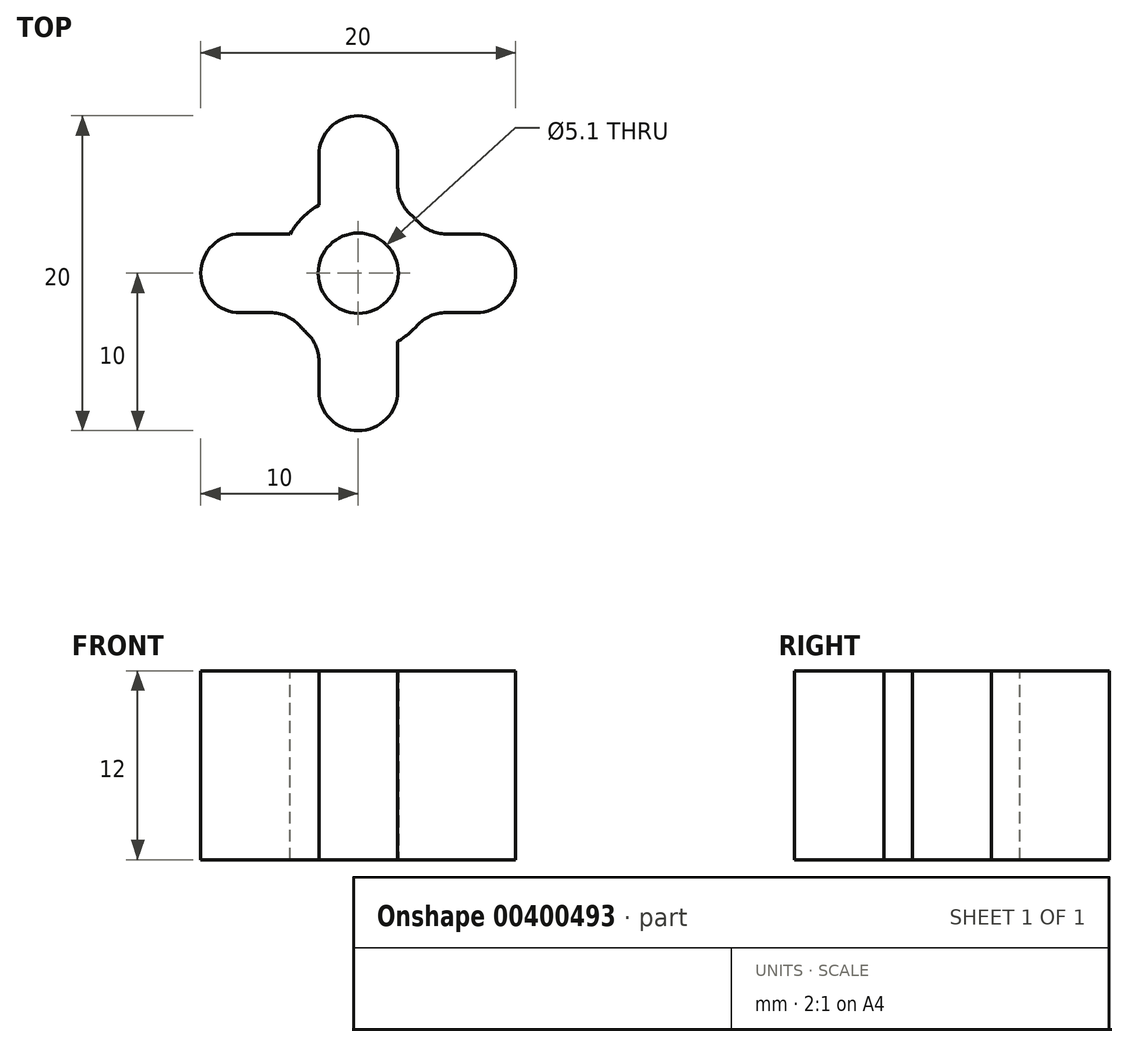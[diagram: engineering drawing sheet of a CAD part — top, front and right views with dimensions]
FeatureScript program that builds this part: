
annotation { "Feature Type Name" : "Feature", "Feature Type Description" : "" }
export const myFeature = defineFeature(function(context is Context, id is Id, definition is map)
    precondition{}
    {
        {
            var Q0;
            Q0=qCreatedBy(makeId("Top.planeOp"),FACE);
            var sketch = newSketch(context, id + "F0", { "sketchPlane" : qUnion([Q0])});
            skCircle(sketch, "E0", {"center": v(0, 0) * mm, "radius": 2.55 * mm});
            skCircle(sketch, "E1", {"center": v(0, 0) * mm, "radius": 5 * mm});
            skSolve(sketch);
        }
        {
            var Q0;
            Q0 = qSketchRegion(id + "F0", true);
            extrude(context, id + "F1", {"entities" : qUnion([Q0]), "depth" : 12 * mm});
        }
        {
            var Q0;
            Q0=makeQuery(id+"F1.opExtrude","CAP_FACE",FACE,{"disambiguationData":[OSD([sQuery(id+"F0.wireOp",EDGE,"E0"),sQuery(id+"F0.wireOp",EDGE,"E1")])],"isStart":false});
            var sketch = newSketch(context, id + "F2", { "sketchPlane" : qUnion([Q0])});
            skLineSegment(sketch, "E2.bottom", {"start": v(-2.5, 4.33) * mm, "end": v(2.5, 4.33) * mm});
            skLineSegment(sketch, "E2.top", {"start": v(-2.5, 10) * mm, "end": v(2.5, 10) * mm});
            skLineSegment(sketch, "E2.left", {"start": v(-2.5, 4.33) * mm, "end": v(-2.5, 10) * mm});
            skLineSegment(sketch, "E2.right", {"start": v(2.5, 4.33) * mm, "end": v(2.5, 10) * mm});
            skLineSegment(sketch, "E3.1.0", {"start": v(-4.33, -2.5) * mm, "end": v(-4.33, 2.5) * mm});
            skLineSegment(sketch, "E3.1.1", {"start": v(-10, -2.5) * mm, "end": v(-10, 2.5) * mm});
            skLineSegment(sketch, "E3.1.2", {"start": v(-4.33, -2.5) * mm, "end": v(-10, -2.5) * mm});
            skLineSegment(sketch, "E3.1.3", {"start": v(-4.33, 2.5) * mm, "end": v(-10, 2.5) * mm});
            skLineSegment(sketch, "E3.2.0", {"start": v(2.5, -4.33) * mm, "end": v(-2.5, -4.33) * mm});
            skLineSegment(sketch, "E3.2.1", {"start": v(2.5, -10) * mm, "end": v(-2.5, -10) * mm});
            skLineSegment(sketch, "E3.2.2", {"start": v(2.5, -4.33) * mm, "end": v(2.5, -10) * mm});
            skLineSegment(sketch, "E3.2.3", {"start": v(-2.5, -4.33) * mm, "end": v(-2.5, -10) * mm});
            skLineSegment(sketch, "E3.3.0", {"start": v(4.33, 2.5) * mm, "end": v(4.33, -2.5) * mm});
            skLineSegment(sketch, "E3.3.1", {"start": v(10, 2.5) * mm, "end": v(10, -2.5) * mm});
            skLineSegment(sketch, "E3.3.2", {"start": v(4.33, 2.5) * mm, "end": v(10, 2.5) * mm});
            skLineSegment(sketch, "E3.3.3", {"start": v(4.33, -2.5) * mm, "end": v(10, -2.5) * mm});
            skPoint(sketch, "E3.center", {"position": v(0, 0) * mm});
            skSolve(sketch);
        }
        {
            var Q0;
            Q0=makeQuery(id+"F2.imprint","IMPRINT",FACE,{"disambiguationData":[TD([[makeQuery(id+"F2.imprint","IMPRINT",EDGE,{"derivedFrom":sQuery(id+"F2.wireOp",EDGE,"E2.top")}),-1.0]])]});
            var Q1;
            Q1=makeQuery(id+"F2.imprint","IMPRINT",FACE,{"disambiguationData":[TD([[makeQuery(id+"F2.imprint","IMPRINT",EDGE,{"derivedFrom":sQuery(id+"F2.wireOp",EDGE,"E3.3.1")}),-1.0]])]});
            var Q2;
            Q2=makeQuery(id+"F2.imprint","IMPRINT",FACE,{"disambiguationData":[TD([[makeQuery(id+"F2.imprint","IMPRINT",EDGE,{"derivedFrom":sQuery(id+"F2.wireOp",EDGE,"E3.2.1")}),-1.0]])]});
            var Q3;
            Q3=makeQuery(id+"F2.imprint","IMPRINT",FACE,{"disambiguationData":[TD([[makeQuery(id+"F2.imprint","IMPRINT",EDGE,{"derivedFrom":sQuery(id+"F2.wireOp",EDGE,"E3.1.1")}),-1.0]])]});
            extrude(context, id + "F3", {"entities" : qUnion([Q0, Q1, Q2, Q3]), "operationType" : NewBodyOperationType.ADD, "oppositeDirection" : true, "depth" : 12 * mm});
        }
        {
            var Q0;
            Q0=makeQuery(id+"F3.opExtrude","SWEPT_EDGE",EDGE,{"disambiguationData":[OSD([sQuery(id+"F2.wireOp",EDGE,"E3.2.1"),sQuery(id+"F2.wireOp",EDGE,"E3.2.2")])]});
            var Q1;
            Q1=makeQuery(id+"F3.opExtrude","SWEPT_EDGE",EDGE,{"disambiguationData":[OSD([sQuery(id+"F2.wireOp",EDGE,"E3.3.1"),sQuery(id+"F2.wireOp",EDGE,"E3.3.3")])]});
            var Q2;
            Q2=makeQuery(id+"F3.opExtrude","SWEPT_EDGE",EDGE,{"disambiguationData":[OSD([sQuery(id+"F2.wireOp",EDGE,"E3.1.1"),sQuery(id+"F2.wireOp",EDGE,"E3.1.2")])]});
            var Q3;
            Q3=makeQuery(id+"F3.opExtrude","SWEPT_EDGE",EDGE,{"disambiguationData":[OSD([sQuery(id+"F2.wireOp",EDGE,"E3.2.1"),sQuery(id+"F2.wireOp",EDGE,"E3.2.3")])]});
            var Q4;
            Q4=makeQuery(id+"F3.opExtrude","SWEPT_EDGE",EDGE,{"disambiguationData":[OSD([sQuery(id+"F2.wireOp",EDGE,"E3.1.1"),sQuery(id+"F2.wireOp",EDGE,"E3.1.3")])]});
            var Q5;
            Q5=makeQuery(id+"F3.opExtrude","SWEPT_EDGE",EDGE,{"disambiguationData":[OSD([sQuery(id+"F2.wireOp",EDGE,"E2.top"),sQuery(id+"F2.wireOp",EDGE,"E2.left")])]});
            var Q6;
            Q6=makeQuery(id+"F3.opExtrude","SWEPT_EDGE",EDGE,{"disambiguationData":[OSD([sQuery(id+"F2.wireOp",EDGE,"E3.3.1"),sQuery(id+"F2.wireOp",EDGE,"E3.3.2")])]});
            var Q7;
            Q7=makeQuery(id+"F3.opExtrude","SWEPT_EDGE",EDGE,{"disambiguationData":[OSD([sQuery(id+"F2.wireOp",EDGE,"E2.top"),sQuery(id+"F2.wireOp",EDGE,"E2.right")])]});
            var Q8;
            Q8=makeQuery(id+"F3.opExtrude","SWEPT_EDGE",EDGE,{"disambiguationData":[OSD([sQuery(id+"F0.wireOp",EDGE,"E1"),sQuery(id+"F2.wireOp",EDGE,"E2.bottom"),sQuery(id+"F2.wireOp",EDGE,"E2.right")])]});
            var Q9;
            Q9=makeQuery(id+"F3.opExtrude","SWEPT_EDGE",EDGE,{"disambiguationData":[OSD([sQuery(id+"F0.wireOp",EDGE,"E1"),sQuery(id+"F2.wireOp",EDGE,"E3.3.0"),sQuery(id+"F2.wireOp",EDGE,"E3.3.2")])]});
            var Q10;
            Q10=makeQuery(id+"F3.opExtrude","SWEPT_EDGE",EDGE,{"disambiguationData":[OSD([sQuery(id+"F0.wireOp",EDGE,"E1"),sQuery(id+"F2.wireOp",EDGE,"E3.3.0"),sQuery(id+"F2.wireOp",EDGE,"E3.3.3")])]});
            var Q11;
            Q11=makeQuery(id+"F3.opExtrude","SWEPT_EDGE",EDGE,{"disambiguationData":[OSD([sQuery(id+"F0.wireOp",EDGE,"E1"),sQuery(id+"F2.wireOp",EDGE,"E2.bottom"),sQuery(id+"F2.wireOp",EDGE,"E2.left")])]});
            var Q12;
            Q12=makeQuery(id+"F3.opExtrude","SWEPT_EDGE",EDGE,{"disambiguationData":[OSD([sQuery(id+"F0.wireOp",EDGE,"E1"),sQuery(id+"F2.wireOp",EDGE,"E3.1.0"),sQuery(id+"F2.wireOp",EDGE,"E3.1.3")])]});
            var Q13;
            Q13=makeQuery(id+"F3.opExtrude","SWEPT_EDGE",EDGE,{"disambiguationData":[OSD([sQuery(id+"F0.wireOp",EDGE,"E1"),sQuery(id+"F2.wireOp",EDGE,"E3.2.0"),sQuery(id+"F2.wireOp",EDGE,"E3.2.3")])]});
            var Q14;
            Q14=makeQuery(id+"F3.opExtrude","SWEPT_EDGE",EDGE,{"disambiguationData":[OSD([sQuery(id+"F0.wireOp",EDGE,"E1"),sQuery(id+"F2.wireOp",EDGE,"E3.1.0"),sQuery(id+"F2.wireOp",EDGE,"E3.1.2")])]});
            fillet(context, id + "F4", {"entities" : qUnion([Q0, Q1, Q2, Q3, Q4, Q5, Q6, Q7, Q8, Q9, Q10, Q11, Q12, Q13, Q14]), "radius" : 2.5 * mm, "tangentPropagation" : true, "allowEdgeOverflow" : false});
        }
    });
